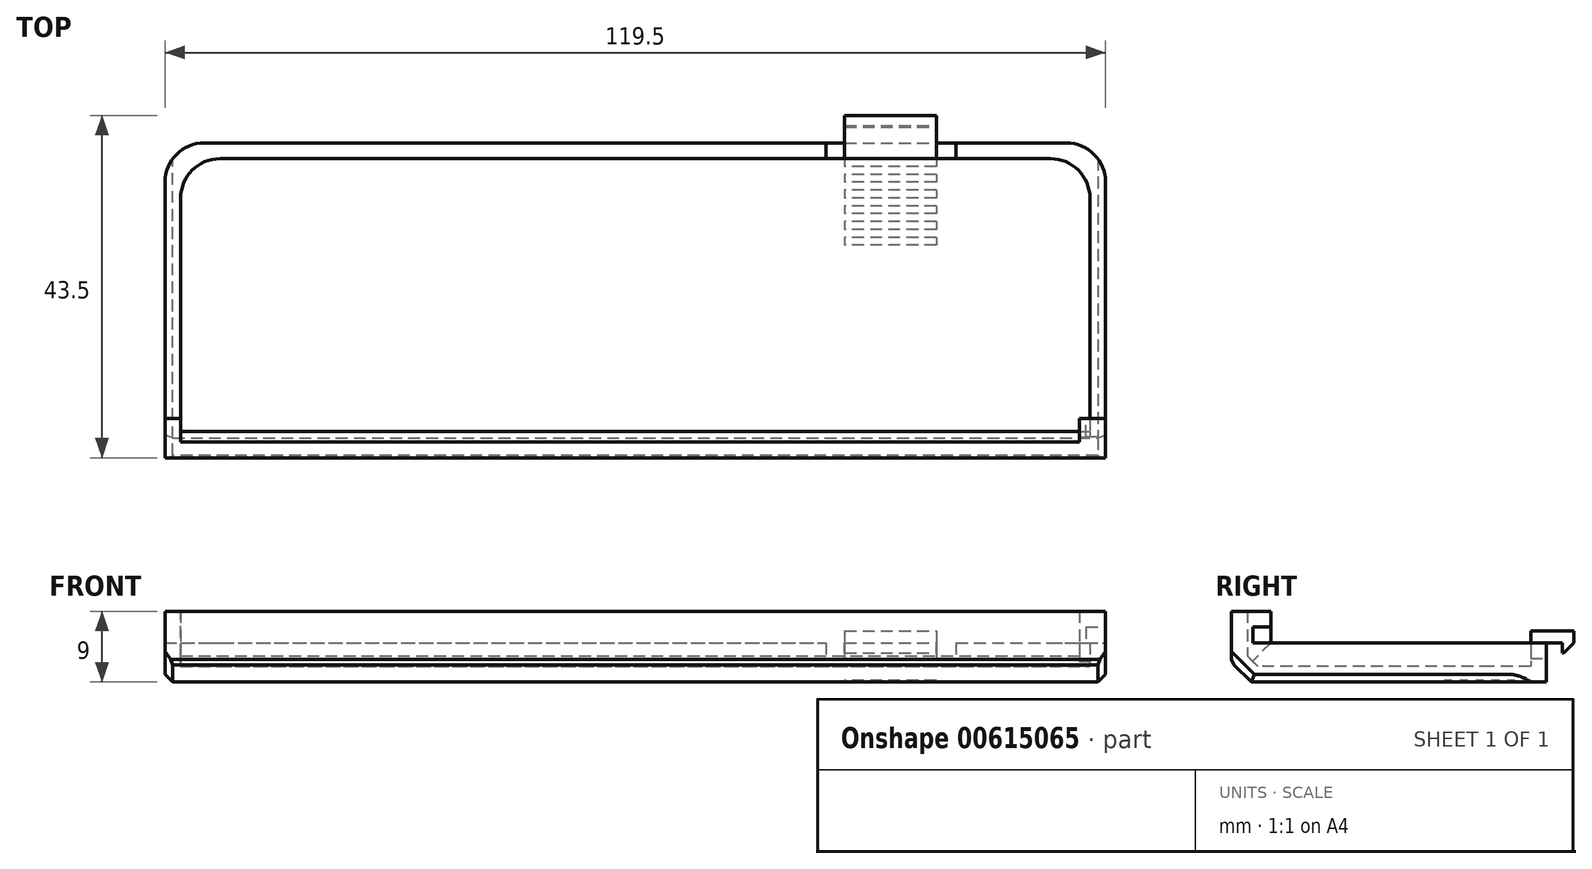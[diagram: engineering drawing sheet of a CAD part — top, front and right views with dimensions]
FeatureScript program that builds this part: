
annotation { "Feature Type Name" : "Feature", "Feature Type Description" : "" }
export const myFeature = defineFeature(function(context is Context, id is Id, definition is map)
    precondition{}
    {
        {
            var Q0;
            Q0=qCreatedBy(makeId("Right.planeOp"),FACE);
            var sketch = newSketch(context, id + "F0", { "sketchPlane" : qUnion([Q0])});
            skLineSegment(sketch, "E0", {"start": v(18.75, 0) * mm, "end": v(-18.75, 0) * mm});
            skLineSegment(sketch, "E1", {"start": v(-18.75, 0) * mm, "end": v(-21.25, 2.5) * mm});
            skLineSegment(sketch, "E2", {"start": v(-21.25, 2.5) * mm, "end": v(-21.25, 9) * mm});
            skLineSegment(sketch, "E3", {"start": v(-21.25, 9) * mm, "end": v(-16.25, 9) * mm});
            skLineSegment(sketch, "E4", {"start": v(-16.25, 9) * mm, "end": v(-16.25, 5) * mm});
            skLineSegment(sketch, "E5", {"start": v(-16.25, 5) * mm, "end": v(16.75, 5) * mm});
            skLineSegment(sketch, "E6", {"start": v(16.75, 5) * mm, "end": v(16.75, 6.5) * mm});
            skLineSegment(sketch, "E7", {"start": v(16.75, 6.5) * mm, "end": v(22.25, 6.5) * mm});
            skLineSegment(sketch, "E8", {"start": v(22.25, 6.5) * mm, "end": v(22.25, 5) * mm});
            skLineSegment(sketch, "E9", {"start": v(22.25, 5) * mm, "end": v(20.95, 3.7) * mm});
            skLineSegment(sketch, "E10", {"start": v(20.95, 3.7) * mm, "end": v(20.75, 3.7) * mm});
            skLineSegment(sketch, "E11", {"start": v(20.75, 3.7) * mm, "end": v(20.75, 5) * mm});
            skLineSegment(sketch, "E12", {"start": v(20.75, 5) * mm, "end": v(18.75, 5) * mm});
            skLineSegment(sketch, "E13", {"start": v(18.75, 5) * mm, "end": v(18.75, 0) * mm});
            skLineSegment(sketch, "E14", {"start": v(16.75, 5) * mm, "end": v(18.75, 5) * mm});
            skLineSegment(sketch, "E15", {"start": v(-16.25, 7) * mm, "end": v(-18.55, 7) * mm});
            skLineSegment(sketch, "E16", {"start": v(-18.55, 7) * mm, "end": v(-18.55, 5) * mm});
            skLineSegment(sketch, "E17", {"start": v(-18.55, 5) * mm, "end": v(-16.25, 5) * mm});
            skLineSegment(sketch, "E18", {"start": v(-16.25, 5) * mm, "end": v(-20, 1.25) * mm});
            skLineSegment(sketch, "E19", {"start": v(16.75, 5) * mm, "end": v(16.75, 3) * mm});
            skLineSegment(sketch, "E20", {"start": v(16.75, 3) * mm, "end": v(18.75, 3) * mm});
            skSolve(sketch);
        }
        {
            var Q0;
            {var subQ2=sQuery(id+"F0.wireOp",EDGE,"E15");Q0=makeQuery(id+"F0.imprint","IMPRINT",FACE,{"disambiguationData":[TD([[makeQuery(id+"F0.imprint","IMPRINT",EDGE,{"derivedFrom":subQ2}),1.0]])]});}
            var Q1;
            {var subQ3=sQuery(id+"F0.wireOp",EDGE,"E2");Q1=makeQuery(id+"F0.imprint","IMPRINT",FACE,{"disambiguationData":[TD([[makeQuery(id+"F0.imprint","IMPRINT",EDGE,{"derivedFrom":subQ3}),-1.0]])]});}
            var Q2;
            {var subQ1=sQuery(id+"F0.wireOp",EDGE,"E0");Q2=makeQuery(id+"F0.imprint","IMPRINT",FACE,{"disambiguationData":[TD([[makeQuery(id+"F0.imprint","IMPRINT",EDGE,{"derivedFrom":subQ1}),-1.0]])]});}
            var Q3;
            {var subQ0=sQuery(id+"F0.wireOp",EDGE,"E14");Q3=makeQuery(id+"F0.imprint","IMPRINT",FACE,{"disambiguationData":[TD([[makeQuery(id+"F0.imprint","IMPRINT",EDGE,{"derivedFrom":subQ0}),-1.0]])]});}
            extrude(context, id + "F1", {"entities" : qUnion([Q0, Q1, Q2, Q3]), "oppositeDirection" : true, "depth" : 119.5 * mm});
        }
        {
            var Q0;
            Q0=makeQuery(id+"F1.opExtrude","SWEPT_FACE",FACE,{"disambiguationData":[OSD([sQuery(id+"F0.wireOp",EDGE,"E5"),sQuery(id+"F0.wireOp",EDGE,"E14")])]});
            var Q1;
            Q1=makeQuery(id+"F1.opExtrude","SWEPT_FACE",FACE,{"disambiguationData":[OSD([sQuery(id+"F0.wireOp",EDGE,"E4")])]});
            var Q2;
            Q2=makeQuery(id+"F1.opExtrude","SWEPT_FACE",FACE,{"disambiguationData":[OSD([sQuery(id+"F0.wireOp",EDGE,"E3")])]});
            shell(context, id + "F2", {"entities" : qUnion([Q0, Q1, Q2]), "thickness" : 2 * mm});
        }
        {
            var Q0;
            {var subQ2=sQuery(id+"F0.wireOp",EDGE,"E15");Q0=makeQuery(id+"F0.imprint","IMPRINT",FACE,{"disambiguationData":[TD([[makeQuery(id+"F0.imprint","IMPRINT",EDGE,{"derivedFrom":subQ2}),1.0]])]});}
            var Q1;
            {var subQ3=sQuery(id+"F0.wireOp",EDGE,"E2");Q1=makeQuery(id+"F0.imprint","IMPRINT",FACE,{"disambiguationData":[TD([[makeQuery(id+"F0.imprint","IMPRINT",EDGE,{"derivedFrom":subQ3}),-1.0]])]});}
            extrude(context, id + "F3", {"entities" : qUnion([Q0, Q1]), "operationType" : NewBodyOperationType.ADD, "oppositeDirection" : true, "depth" : 3.35 * mm});
        }
        {
            var Q0;
            {var subQ2=sQuery(id+"F0.wireOp",EDGE,"E15");Q0=makeQuery(id+"F0.imprint","IMPRINT",FACE,{"disambiguationData":[TD([[makeQuery(id+"F0.imprint","IMPRINT",EDGE,{"derivedFrom":subQ2}),1.0]])]});}
            extrude(context, id + "F4", {"entities" : qUnion([Q0]), "operationType" : NewBodyOperationType.REMOVE, "oppositeDirection" : true, "depth" : 2.5 * mm});
        }
        {
            var Q0;
            {var subQ0=sQuery(id+"F0.wireOp",EDGE,"E14");Q0=makeQuery(id+"F0.imprint","IMPRINT",FACE,{"disambiguationData":[TD([[makeQuery(id+"F0.imprint","IMPRINT",EDGE,{"derivedFrom":subQ0}),-1.0]])]});}
            extrude(context, id + "F5", {"entities" : qUnion([Q0]), "operationType" : NewBodyOperationType.REMOVE, "oppositeDirection" : true, "depth" : (16.5 + 19) * mm, "hasSecondDirection" : true, "secondDirectionOppositeDirection" : true, "secondDirectionDepth" : 19 * mm});
        }
        {
            var Q0;
            {var subQ0=sQuery(id+"F0.wireOp",EDGE,"E14");Q0=makeQuery(id+"F0.imprint","IMPRINT",FACE,{"disambiguationData":[TD([[makeQuery(id+"F0.imprint","IMPRINT",EDGE,{"derivedFrom":subQ0}),-1.0]])]});}
            var Q1;
            Q1=makeQuery(id+"F0.imprint","IMPRINT",FACE,{"disambiguationData":[TD([[makeQuery(id+"F0.imprint","IMPRINT",EDGE,{"derivedFrom":sQuery(id+"F0.wireOp",EDGE,"E6")}),-1.0]])]});
            extrude(context, id + "F6", {"entities" : qUnion([Q0, Q1]), "operationType" : NewBodyOperationType.ADD, "oppositeDirection" : true, "depth" : 33.15 * mm, "hasSecondDirection" : true, "secondDirectionOppositeDirection" : true, "secondDirectionDepth" : 21.5 * mm});
        }
        {
            var Q0;
            Q0=makeQuery(id+"F1.opExtrude","CAP_FACE",FACE,{"disambiguationData":[OSD([sQuery(id+"F0.wireOp",EDGE,"E0"),sQuery(id+"F0.wireOp",EDGE,"E1"),sQuery(id+"F0.wireOp",EDGE,"E2"),sQuery(id+"F0.wireOp",EDGE,"E3"),sQuery(id+"F0.wireOp",EDGE,"E4"),sQuery(id+"F0.wireOp",EDGE,"E5"),sQuery(id+"F0.wireOp",EDGE,"E13"),sQuery(id+"F0.wireOp",EDGE,"E14")])],"isStart":true});
            var Q1;
            Q1=makeQuery(id+"F1.opExtrude","CAP_FACE",FACE,{"disambiguationData":[OSD([sQuery(id+"F0.wireOp",EDGE,"E0"),sQuery(id+"F0.wireOp",EDGE,"E1"),sQuery(id+"F0.wireOp",EDGE,"E2"),sQuery(id+"F0.wireOp",EDGE,"E3"),sQuery(id+"F0.wireOp",EDGE,"E4"),sQuery(id+"F0.wireOp",EDGE,"E5"),sQuery(id+"F0.wireOp",EDGE,"E13"),sQuery(id+"F0.wireOp",EDGE,"E14")])],"isStart":false});
            cPlane(context, id + "F7", {"entities" : qUnion([Q0, Q1]), "cplaneType" : CPlaneType.MID_PLANE, "offset" : 25 * mm, "width" : 150 * mm, "height" : 150 * mm});
        }
        {
            var Q0;
            Q0=makeQuery(id+"F1.opExtrude","SWEPT_FACE",FACE,{"disambiguationData":[OSD([sQuery(id+"F0.wireOp",EDGE,"E0")])]});
            var sketch = newSketch(context, id + "F8", { "sketchPlane" : qUnion([Q0])});
            skLineSegment(sketch, "E21.bottom", {"start": v(-21.5, -16.75) * mm, "end": v(-33.15, -16.75) * mm});
            skLineSegment(sketch, "E21.top", {"start": v(-21.5, -15.75) * mm, "end": v(-33.15, -15.75) * mm});
            skLineSegment(sketch, "E21.left", {"start": v(-21.5, -16.75) * mm, "end": v(-21.5, -15.75) * mm});
            skLineSegment(sketch, "E21.right", {"start": v(-33.15, -16.75) * mm, "end": v(-33.15, -15.75) * mm});
            skLineSegment(sketch, "E22.0.1.0", {"start": v(-21.5, -13.75) * mm, "end": v(-33.15, -13.75) * mm});
            skLineSegment(sketch, "E22.0.1.1", {"start": v(-21.5, -14.75) * mm, "end": v(-33.15, -14.75) * mm});
            skLineSegment(sketch, "E22.0.1.2", {"start": v(-33.15, -14.75) * mm, "end": v(-33.15, -13.75) * mm});
            skLineSegment(sketch, "E22.0.1.3", {"start": v(-21.5, -14.75) * mm, "end": v(-21.5, -13.75) * mm});
            skLineSegment(sketch, "E22.0.2.0", {"start": v(-21.5, -11.75) * mm, "end": v(-33.15, -11.75) * mm});
            skLineSegment(sketch, "E22.0.2.1", {"start": v(-21.5, -12.75) * mm, "end": v(-33.15, -12.75) * mm});
            skLineSegment(sketch, "E22.0.2.2", {"start": v(-33.15, -12.75) * mm, "end": v(-33.15, -11.75) * mm});
            skLineSegment(sketch, "E22.0.2.3", {"start": v(-21.5, -12.75) * mm, "end": v(-21.5, -11.75) * mm});
            skLineSegment(sketch, "E22.0.3.0", {"start": v(-21.5, -9.75) * mm, "end": v(-33.15, -9.75) * mm});
            skLineSegment(sketch, "E22.0.3.1", {"start": v(-21.5, -10.75) * mm, "end": v(-33.15, -10.75) * mm});
            skLineSegment(sketch, "E22.0.3.2", {"start": v(-33.15, -10.75) * mm, "end": v(-33.15, -9.75) * mm});
            skLineSegment(sketch, "E22.0.3.3", {"start": v(-21.5, -10.75) * mm, "end": v(-21.5, -9.75) * mm});
            skLineSegment(sketch, "E22.0.4.0", {"start": v(-21.5, -7.75) * mm, "end": v(-33.15, -7.75) * mm});
            skLineSegment(sketch, "E22.0.4.1", {"start": v(-21.5, -8.75) * mm, "end": v(-33.15, -8.75) * mm});
            skLineSegment(sketch, "E22.0.4.2", {"start": v(-33.15, -8.75) * mm, "end": v(-33.15, -7.75) * mm});
            skLineSegment(sketch, "E22.0.4.3", {"start": v(-21.5, -8.75) * mm, "end": v(-21.5, -7.75) * mm});
            skLineSegment(sketch, "E22.0.5.0", {"start": v(-21.5, -5.75) * mm, "end": v(-33.15, -5.75) * mm});
            skLineSegment(sketch, "E22.0.5.1", {"start": v(-21.5, -6.75) * mm, "end": v(-33.15, -6.75) * mm});
            skLineSegment(sketch, "E22.0.5.2", {"start": v(-33.15, -6.75) * mm, "end": v(-33.15, -5.75) * mm});
            skLineSegment(sketch, "E22.0.5.3", {"start": v(-21.5, -6.75) * mm, "end": v(-21.5, -5.75) * mm});
            skLineSegment(sketch, "E22.direction1", {"start": v(-33.15, -16.75) * mm, "end": v(-8.15, -16.75) * mm, "construction": true});
            skLineSegment(sketch, "E22.direction2", {"start": v(-33.15, -16.75) * mm, "end": v(-33.15, -14.75) * mm, "construction": true});
            skSolve(sketch);
        }
        {
            var Q0;
            Q0=qSketchRegion(id+"F8",true);
            extrude(context, id + "F9", {"entities" : qUnion([Q0]), "operationType" : NewBodyOperationType.REMOVE, "oppositeDirection" : true, "depth" : (.125 * 2) * mm});
        }
        {
            var Q0;
            Q0=makeQuery(id+"F1.opExtrude","CAP_EDGE",EDGE,{"disambiguationData":[OSD([sQuery(id+"F0.wireOp",EDGE,"E0")])],"isStart":true});
            var Q1;
            Q1=makeQuery(id+"F1.opExtrude","CAP_EDGE",EDGE,{"disambiguationData":[OSD([sQuery(id+"F0.wireOp",EDGE,"E0")])],"isStart":false});
            var Q2;
            Q2=makeQuery(id+"F1.opExtrude","CAP_EDGE",EDGE,{"disambiguationData":[OSD([sQuery(id+"F0.wireOp",EDGE,"E1")])],"isStart":true});
            var Q3;
            Q3=makeQuery(id+"F1.opExtrude","CAP_EDGE",EDGE,{"disambiguationData":[OSD([sQuery(id+"F0.wireOp",EDGE,"E1")])],"isStart":false});
            var Q4;
            Q4=makeQuery(id+"F1.opExtrude","SWEPT_EDGE",EDGE,{"disambiguationData":[OSD([sQuery(id+"F0.wireOp",EDGE,"E1"),sQuery(id+"F0.wireOp",EDGE,"E2")])]});
            chamfer(context, id + "F10", {"entities" : qUnion([Q0, Q1, Q2, Q3, Q4]), "width" : 1 * mm, "tangentPropagation" : true});
        }
        {
            var Q0;
            Q0=makeQuery(id+"F1.opExtrude","CAP_EDGE",EDGE,{"disambiguationData":[OSD([sQuery(id+"F0.wireOp",EDGE,"E13")])],"isStart":true});
            var Q1;
            {var subQ0=sQuery(id+"F0.wireOp",EDGE,"E13");Q1=makeQuery(id+"F2.opShell","OFFSET_EDGE",EDGE,{"disambiguationData":[OSD([subQ0]),TDD([makeQuery(id+"F1.opExtrude","CAP_EDGE",EDGE,{"disambiguationData":[OSD([subQ0])],"isStart":true})])]});}
            var Q2;
            {var subQ0=sQuery(id+"F0.wireOp",EDGE,"E13");Q2=makeQuery(id+"F2.opShell","OFFSET_EDGE",EDGE,{"disambiguationData":[OSD([subQ0]),TDD([makeQuery(id+"F1.opExtrude","CAP_EDGE",EDGE,{"disambiguationData":[OSD([subQ0])],"isStart":false})])]});}
            var Q3;
            Q3=makeQuery(id+"F1.opExtrude","CAP_EDGE",EDGE,{"disambiguationData":[OSD([sQuery(id+"F0.wireOp",EDGE,"E13")])],"isStart":false});
            fillet(context, id + "F11", {"entities" : qUnion([Q0, Q1, Q2, Q3]), "radius" : 5 * mm, "tangentPropagation" : true, "allowEdgeOverflow" : false});
        }
    });
